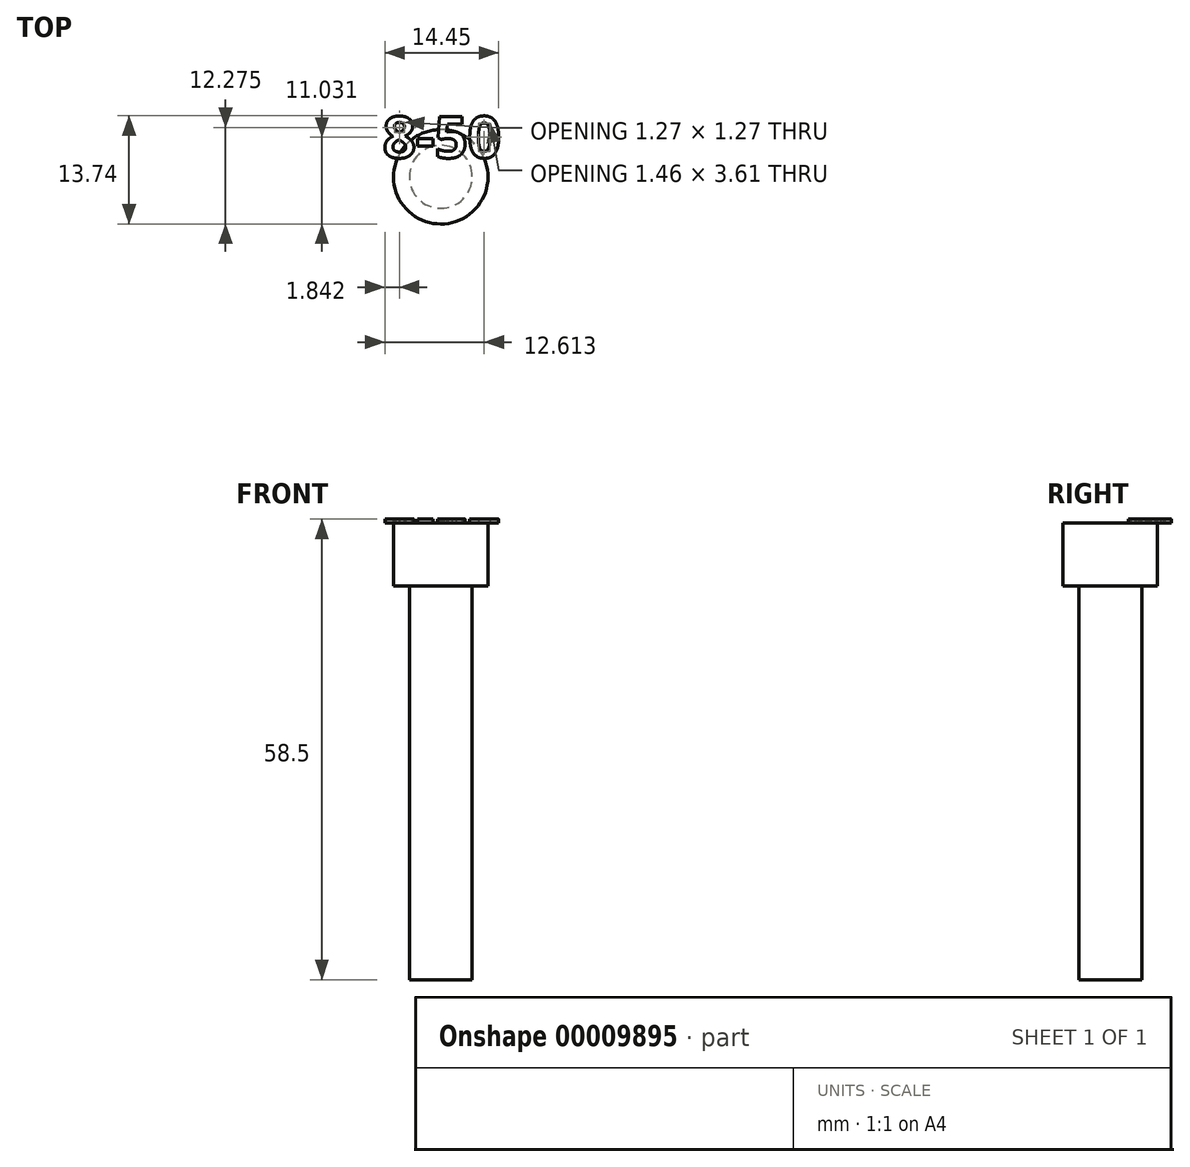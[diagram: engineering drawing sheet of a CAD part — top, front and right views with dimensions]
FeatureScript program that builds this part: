
annotation { "Feature Type Name" : "Feature", "Feature Type Description" : "" }
export const myFeature = defineFeature(function(context is Context, id is Id, definition is map)
    precondition{}
    {
        {
            var Q0;
            Q0=qCreatedBy(makeId("Top.planeOp"),FACE);
            var sketch = newSketch(context, id + "F0", { "sketchPlane" : qUnion([Q0])});
            skCircle(sketch, "E0", {"center": v(0, 0) * mm, "radius": 4 * mm});
            skSolve(sketch);
        }
        {
            var Q0;
            Q0=qSketchRegion(id+"F0",true);
            extrude(context, id + "F1", {"entities" : qUnion([Q0]), "depth" : 50 * mm});
        }
        {
            var Q0;
            Q0=makeQuery(id+"F1.opExtrude","CAP_FACE",FACE,{"disambiguationData":[OSD([sQuery(id+"F0.wireOp",EDGE,"E0")])],"isStart":false});
            var sketch = newSketch(context, id + "F2", { "sketchPlane" : qUnion([Q0])});
            skCircle(sketch, "E1", {"center": v(0, 0) * mm, "radius": 6 * mm});
            skSolve(sketch);
        }
        {
            var Q0;
            Q0=qSketchRegion(id+"F2",true);
            extrude(context, id + "F3", {"entities" : qUnion([Q0]), "operationType" : NewBodyOperationType.ADD, "depth" : 8 * mm});
        }
        {
            var Q0;
            Q0=makeQuery(id+"F3.opExtrude","CAP_FACE",FACE,{"disambiguationData":[OSD([sQuery(id+"F2.wireOp",EDGE,"E1")])],"isStart":false});
            var sketch = newSketch(context, id + "F4", { "sketchPlane" : qUnion([Q0]), "asVersion" : FeatureScriptVersionNumber.V307_HOLE_FEATURE_FIX_UNDETERMINED_TARGET_BODY_2});
            skText(sketch, "E2", { "text": "8-50", "fontName": "OpenSans-Bold.ttf"});
            const initialGuessF4  = {"E2": [-0.00736, 0.0024, 1, 0, 0.0053]};
            skSetInitialGuess(sketch, initialGuessF4);
            skSolve(sketch);
        }
        {
            var Q0;
            Q0 = qSketchRegion(id + "F4", true);
            extrude(context, id + "F5", {"entities" : qUnion([Q0]), "operationType" : NewBodyOperationType.ADD, "depth" : 0.5 * mm});
        }
    });
